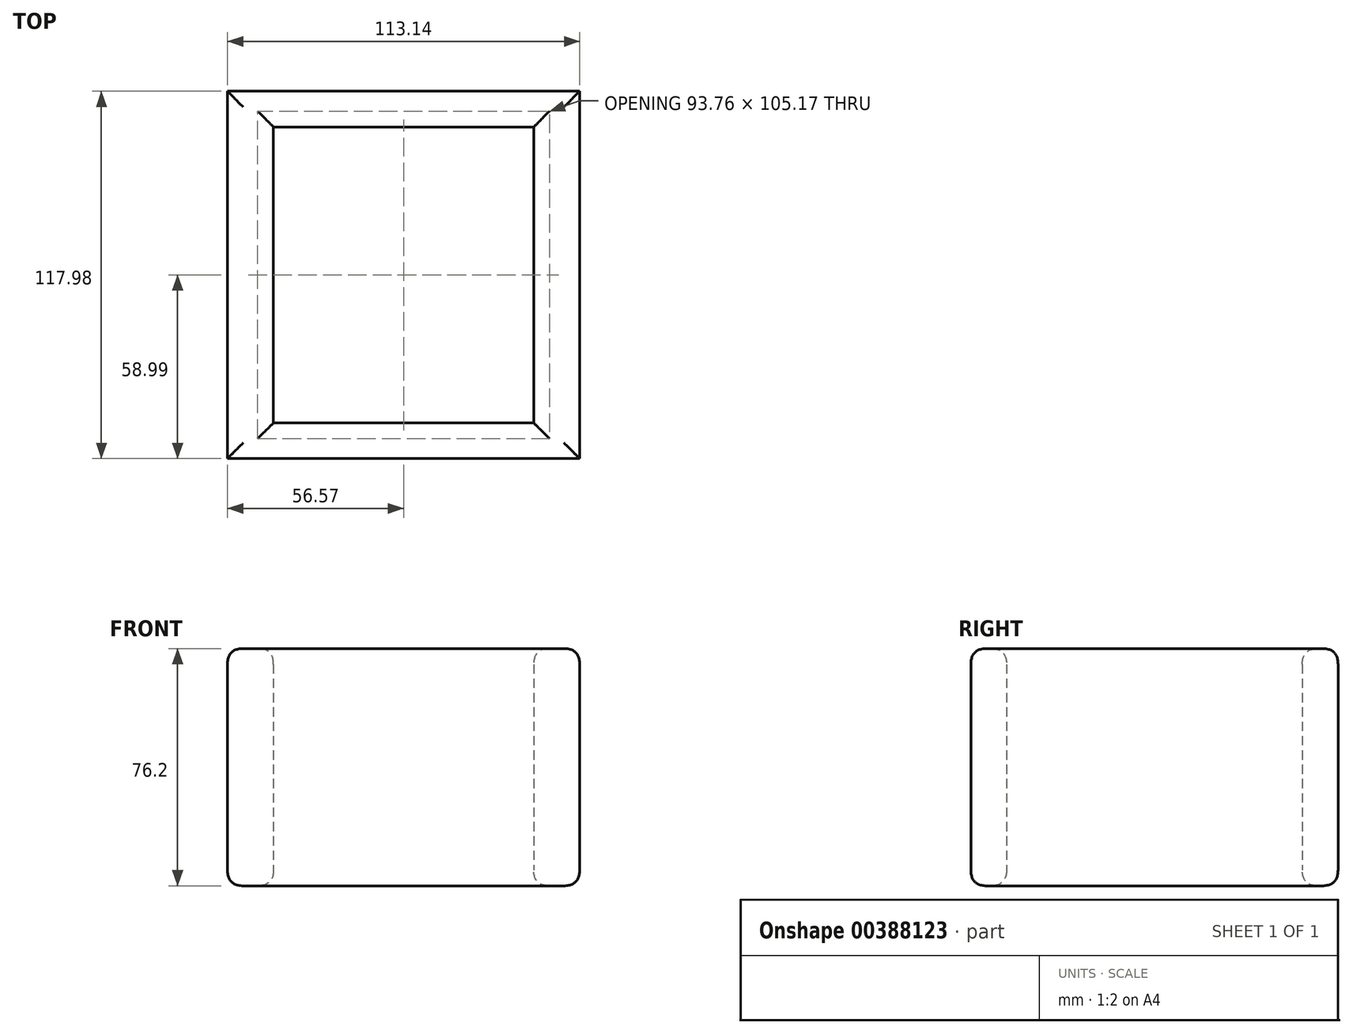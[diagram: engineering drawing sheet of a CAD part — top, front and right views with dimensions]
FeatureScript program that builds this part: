
annotation { "Feature Type Name" : "Feature", "Feature Type Description" : "" }
export const myFeature = defineFeature(function(context is Context, id is Id, definition is map)
    precondition{}
    {
        {
            var Q0;
            Q0=qCreatedBy(makeId("Top.planeOp"),FACE);
            var sketch = newSketch(context, id + "F0", { "sketchPlane" : qUnion([Q0])});
            skLineSegment(sketch, "E0.bottom", {"start": v(56.57, -58.99) * mm, "end": v(-56.57, -58.99) * mm});
            skLineSegment(sketch, "E0.top", {"start": v(56.57, 58.99) * mm, "end": v(-56.57, 58.99) * mm});
            skLineSegment(sketch, "E0.left", {"start": v(56.57, -58.99) * mm, "end": v(56.57, 58.99) * mm});
            skLineSegment(sketch, "E0.right", {"start": v(-56.57, -58.99) * mm, "end": v(-56.57, 58.99) * mm});
            skPoint(sketch, "E0.middle", {"position": v(0, 0) * mm});
            skSolve(sketch);
        }
        {
            var Q0;
            Q0 = qSketchRegion(id + "F0", true);
            extrude(context, id + "F1", {"entities" : qUnion([Q0]), "depth" : 76.2 * mm});
        }
        {
            var Q0;
            Q0=qCreatedBy(makeId("Top.planeOp"),FACE);
            var sketch = newSketch(context, id + "F2", { "sketchPlane" : qUnion([Q0])});
            skLineSegment(sketch, "E1.bottom", {"start": v(-41.8, 47.5) * mm, "end": v(41.8, 47.5) * mm});
            skLineSegment(sketch, "E1.top", {"start": v(-41.8, -47.5) * mm, "end": v(41.8, -47.5) * mm});
            skLineSegment(sketch, "E1.left", {"start": v(-41.8, 47.5) * mm, "end": v(-41.8, -47.5) * mm});
            skLineSegment(sketch, "E1.right", {"start": v(41.8, 47.5) * mm, "end": v(41.8, -47.5) * mm});
            skPoint(sketch, "E1.middle", {"position": v(0, 0) * mm});
            skSolve(sketch);
        }
        {
            var Q0;
            Q0=makeQuery(id+"F2.imprint","IMPRINT",FACE,{"disambiguationData":[TD([[makeQuery(id+"F2.imprint","IMPRINT",EDGE,{"derivedFrom":sQuery(id+"F2.wireOp",EDGE,"E1.bottom")}),-1.0]])]});
            extrude(context, id + "F3", {"entities" : qUnion([Q0]), "operationType" : NewBodyOperationType.REMOVE, "depth" : 105.12 * mm});
        }
        {
            var Q0;
            Q0=makeQuery(id+"F3.boolean.opBoolean","INTERSECT",EDGE,{"derivedFrom":[makeQuery(id+"F1.opExtrude","CAP_FACE",FACE,{"disambiguationData":[OSD([sQuery(id+"F0.wireOp",EDGE,"E0.bottom"),sQuery(id+"F0.wireOp",EDGE,"E0.top"),sQuery(id+"F0.wireOp",EDGE,"E0.left"),sQuery(id+"F0.wireOp",EDGE,"E0.right")])],"isStart":false}),makeQuery(id+"F3.opExtrude","SWEPT_FACE",FACE,{"disambiguationData":[OSD([sQuery(id+"F2.wireOp",EDGE,"E1.top")])]})]});
            var Q1;
            Q1=makeQuery(id+"F3.boolean.opBoolean","INTERSECT",EDGE,{"derivedFrom":[makeQuery(id+"F1.opExtrude","CAP_FACE",FACE,{"disambiguationData":[OSD([sQuery(id+"F0.wireOp",EDGE,"E0.bottom"),sQuery(id+"F0.wireOp",EDGE,"E0.top"),sQuery(id+"F0.wireOp",EDGE,"E0.left"),sQuery(id+"F0.wireOp",EDGE,"E0.right")])],"isStart":false}),makeQuery(id+"F3.opExtrude","SWEPT_FACE",FACE,{"disambiguationData":[OSD([sQuery(id+"F2.wireOp",EDGE,"E1.left")])]})]});
            var Q2;
            Q2=makeQuery(id+"F3.boolean.opBoolean","INTERSECT",EDGE,{"derivedFrom":[makeQuery(id+"F1.opExtrude","CAP_FACE",FACE,{"disambiguationData":[OSD([sQuery(id+"F0.wireOp",EDGE,"E0.bottom"),sQuery(id+"F0.wireOp",EDGE,"E0.top"),sQuery(id+"F0.wireOp",EDGE,"E0.left"),sQuery(id+"F0.wireOp",EDGE,"E0.right")])],"isStart":false}),makeQuery(id+"F3.opExtrude","SWEPT_FACE",FACE,{"disambiguationData":[OSD([sQuery(id+"F2.wireOp",EDGE,"E1.bottom")])]})]});
            var Q3;
            Q3=makeQuery(id+"F3.boolean.opBoolean","INTERSECT",EDGE,{"derivedFrom":[makeQuery(id+"F1.opExtrude","CAP_FACE",FACE,{"disambiguationData":[OSD([sQuery(id+"F0.wireOp",EDGE,"E0.bottom"),sQuery(id+"F0.wireOp",EDGE,"E0.top"),sQuery(id+"F0.wireOp",EDGE,"E0.left"),sQuery(id+"F0.wireOp",EDGE,"E0.right")])],"isStart":false}),makeQuery(id+"F3.opExtrude","SWEPT_FACE",FACE,{"disambiguationData":[OSD([sQuery(id+"F2.wireOp",EDGE,"E1.right")])]})]});
            var Q4;
            Q4=makeQuery(id+"F1.opExtrude","CAP_EDGE",EDGE,{"disambiguationData":[OSD([sQuery(id+"F0.wireOp",EDGE,"E0.top")])],"isStart":false});
            var Q5;
            Q5=makeQuery(id+"F1.opExtrude","CAP_EDGE",EDGE,{"disambiguationData":[OSD([sQuery(id+"F0.wireOp",EDGE,"E0.left")])],"isStart":false});
            var Q6;
            Q6=makeQuery(id+"F1.opExtrude","CAP_EDGE",EDGE,{"disambiguationData":[OSD([sQuery(id+"F0.wireOp",EDGE,"E0.right")])],"isStart":false});
            var Q7;
            Q7=makeQuery(id+"F1.opExtrude","CAP_EDGE",EDGE,{"disambiguationData":[OSD([sQuery(id+"F0.wireOp",EDGE,"E0.bottom")])],"isStart":false});
            var Q8;
            Q8=makeQuery(id+"F1.opExtrude","CAP_FACE",FACE,{"disambiguationData":[OSD([sQuery(id+"F0.wireOp",EDGE,"E0.bottom"),sQuery(id+"F0.wireOp",EDGE,"E0.top"),sQuery(id+"F0.wireOp",EDGE,"E0.left"),sQuery(id+"F0.wireOp",EDGE,"E0.right")])],"isStart":true});
            fillet(context, id + "F4", {"entities" : qUnion([Q0, Q1, Q2, Q3, Q4, Q5, Q6, Q7, Q8]), "radius" : 5.08 * mm, "tangentPropagation" : true, "rho" : 0.5, "crossSection" : FilletCrossSection.CONIC, "allowEdgeOverflow" : false});
        }
    });
